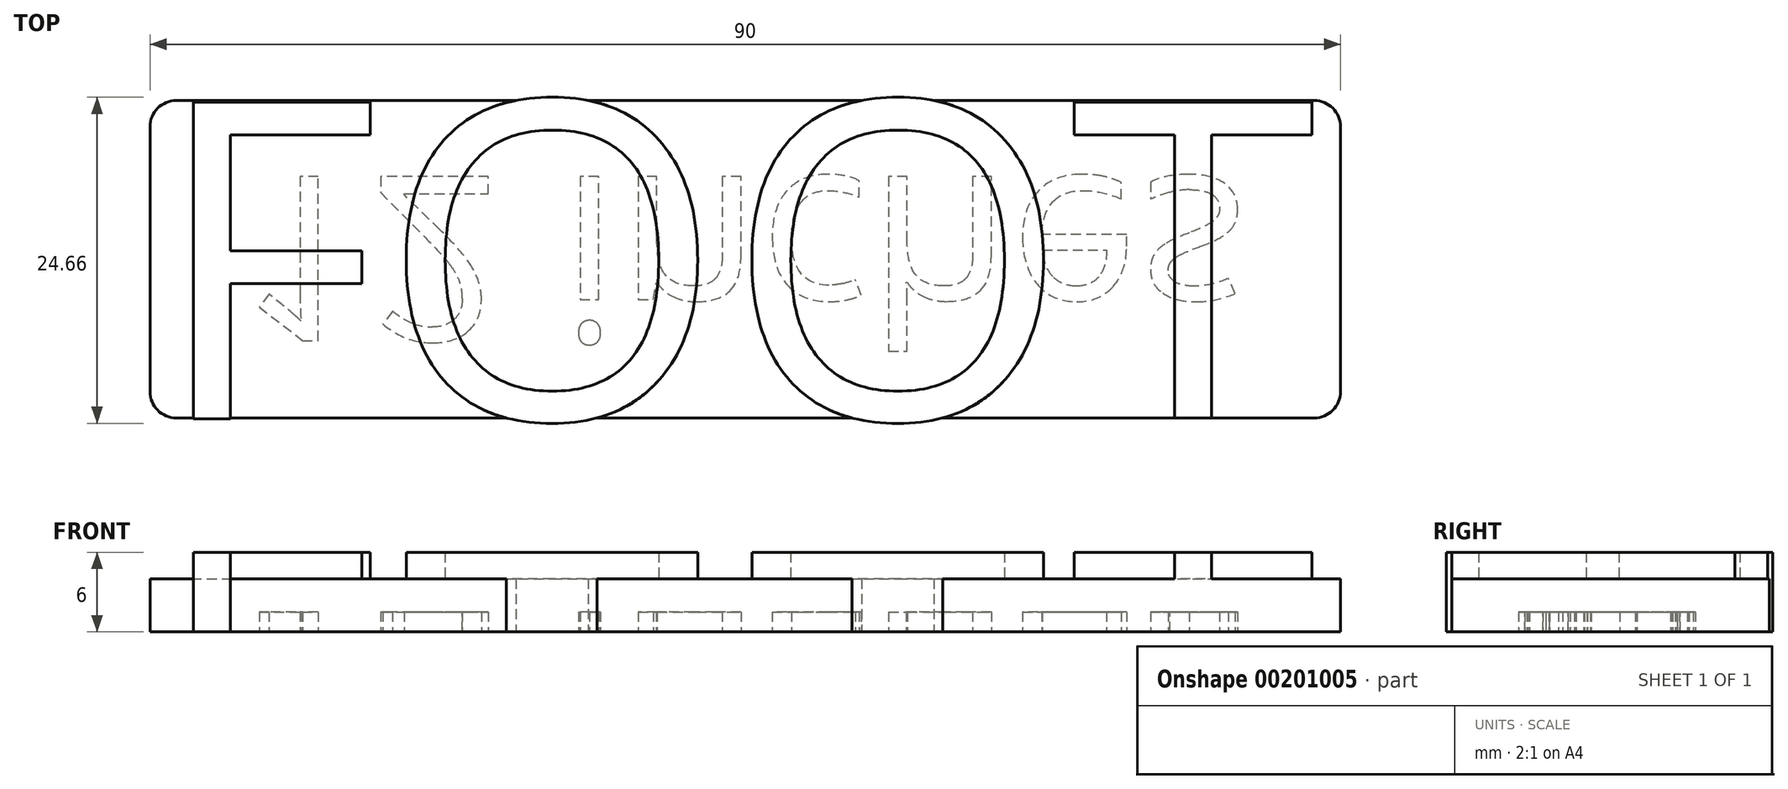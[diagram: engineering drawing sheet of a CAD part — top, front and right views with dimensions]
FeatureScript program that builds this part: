
annotation { "Feature Type Name" : "Feature", "Feature Type Description" : "" }
export const myFeature = defineFeature(function(context is Context, id is Id, definition is map)
    precondition{}
    {
        {
            var Q0;
            Q0=qCreatedBy(makeId("Top.planeOp"),FACE);
            var sketch = newSketch(context, id + "F0", { "sketchPlane" : qUnion([Q0])});
            skLineSegment(sketch, "E0.bottom", {"start": v(-45, 12) * mm, "end": v(45, 12) * mm});
            skLineSegment(sketch, "E0.top", {"start": v(-45, -12) * mm, "end": v(45, -12) * mm});
            skLineSegment(sketch, "E0.left", {"start": v(-45, 12) * mm, "end": v(-45, -12) * mm});
            skLineSegment(sketch, "E0.right", {"start": v(45, 12) * mm, "end": v(45, -12) * mm});
            skLineSegment(sketch, "E1", {"start": v(0, -12) * mm, "end": v(0, 12) * mm, "construction": true});
            skSolve(sketch);
        }
        {
            var Q0;
            Q0=makeQuery(id+"F0.imprint","IMPRINT",FACE,{"disambiguationData":[TD([[makeQuery(id+"F0.imprint","IMPRINT",EDGE,{"derivedFrom":sQuery(id+"F0.wireOp",EDGE,"E0.bottom")}),-1.0]])]});
            extrude(context, id + "F1", {"entities" : qUnion([Q0]), "depth" : 4 * mm});
        }
        {
            var Q0;
            Q0=makeQuery(id+"F1.opExtrude","SWEPT_EDGE",EDGE,{"disambiguationData":[OSD([sQuery(id+"F0.wireOp",EDGE,"E0.top"),sQuery(id+"F0.wireOp",EDGE,"E0.left")])]});
            var Q1;
            Q1=makeQuery(id+"F1.opExtrude","SWEPT_EDGE",EDGE,{"disambiguationData":[OSD([sQuery(id+"F0.wireOp",EDGE,"E0.bottom"),sQuery(id+"F0.wireOp",EDGE,"E0.right")])]});
            var Q2;
            Q2=makeQuery(id+"F1.opExtrude","SWEPT_EDGE",EDGE,{"disambiguationData":[OSD([sQuery(id+"F0.wireOp",EDGE,"E0.bottom"),sQuery(id+"F0.wireOp",EDGE,"E0.left")])]});
            var Q3;
            Q3=makeQuery(id+"F1.opExtrude","SWEPT_EDGE",EDGE,{"disambiguationData":[OSD([sQuery(id+"F0.wireOp",EDGE,"E0.top"),sQuery(id+"F0.wireOp",EDGE,"E0.right")])]});
            fillet(context, id + "F2", {"entities" : qUnion([Q0, Q1, Q2, Q3]), "radius" : 2 * mm, "tangentPropagation" : true, "allowEdgeOverflow" : false});
        }
        {
            var Q0;
            Q0=makeQuery(id+"F1.opExtrude","CAP_FACE",FACE,{"disambiguationData":[OSD([sQuery(id+"F0.wireOp",EDGE,"E0.bottom"),sQuery(id+"F0.wireOp",EDGE,"E0.top"),sQuery(id+"F0.wireOp",EDGE,"E0.left"),sQuery(id+"F0.wireOp",EDGE,"E0.right")])],"isStart":false});
            var sketch = newSketch(context, id + "F3", { "sketchPlane" : qUnion([Q0])});
            skText(sketch, "E2", { "text": "FOOT", "fontName": "OpenSans-Regular.ttf"});
            const initialGuessF3  = {"E2": [-0.045, -0.01208, 1, 0, 0.02416]};
            skSetInitialGuess(sketch, initialGuessF3);
            skSolve(sketch);
        }
        {
            var Q0;
            {var subQ0=sQuery(id+"F3.wireOp",EDGE,"E2.sketch_text.stroke-4");Q0=makeQuery(id+"F3.imprint","IMPRINT",FACE,{"disambiguationData":[TD([[makeQuery(id+"F3.imprint","IMPRINT",EDGE,{"derivedFrom":subQ0}),-1.0]])]});}
            var Q1;
            {var subQ0=sQuery(id+"F3.wireOp",EDGE,"E2.sketch_text.stroke-3");var subQ1=sQuery(id+"F3.wireOp",EDGE,"E2.sketch_text.stroke-2");var subQ2=makeQuery(id+"F3.imprint","INTERSECT",VERTEX,{"derivedFrom":[subQ1,subQ0]});Q1=makeQuery(id+"F3.imprint","IMPRINT",FACE,{"disambiguationData":[TD([[makeQuery(id+"F3.imprint","IMPRINT",EDGE,{"disambiguationData":[TD([[subQ2,1.0]])],"derivedFrom":subQ1}),-1.0]])]});}
            var Q2;
            {var subQ1=sQuery(id+"F3.wireOp",EDGE,"E2.sketch_text.stroke-1");Q2=makeQuery(id+"F3.imprint","IMPRINT",FACE,{"disambiguationData":[TD([[makeQuery(id+"F3.imprint","IMPRINT",EDGE,{"derivedFrom":subQ1}),-1.0]])]});}
            var Q3;
            {var subQ0=sQuery(id+"F3.wireOp",EDGE,"E2.sketch_text.stroke-0");var subQ1=makeQuery(id+"F1.opExtrude","CAP_EDGE",EDGE,{"disambiguationData":[OSD([sQuery(id+"F0.wireOp",EDGE,"E0.top")])],"isStart":false});var subQ2=makeQuery(id+"F3.imprint","INTERSECT",VERTEX,{"derivedFrom":[subQ1,subQ0]});Q3=makeQuery(id+"F3.imprint","IMPRINT",FACE,{"disambiguationData":[TD([[makeQuery(id+"F3.imprint","IMPRINT",EDGE,{"disambiguationData":[TD([[subQ2,-1.0]])],"derivedFrom":subQ0}),-1.0]])]});}
            var Q4;
            {var subQ1=sQuery(id+"F3.wireOp",EDGE,"E2.sketch_text.stroke-8");Q4=makeQuery(id+"F3.imprint","IMPRINT",FACE,{"disambiguationData":[TD([[makeQuery(id+"F3.imprint","IMPRINT",EDGE,{"derivedFrom":subQ1}),-1.0]])]});}
            var Q5;
            {var subQ0=sQuery(id+"F3.wireOp",EDGE,"E2.sketch_text.stroke-9");var subQ1=makeQuery(id+"F1.opExtrude","CAP_EDGE",EDGE,{"disambiguationData":[OSD([sQuery(id+"F0.wireOp",EDGE,"E0.bottom")])],"isStart":false});var subQ2=makeQuery(id+"F3.imprint","INTERSECT",VERTEX,{"derivedFrom":[subQ1,subQ0]});Q5=makeQuery(id+"F3.imprint","IMPRINT",FACE,{"disambiguationData":[TD([[makeQuery(id+"F3.imprint","IMPRINT",EDGE,{"disambiguationData":[TD([[subQ2,1.0]])],"derivedFrom":subQ0}),-1.0]])]});}
            var Q6;
            {var subQ1=sQuery(id+"F3.wireOp",EDGE,"E2.sketch_text.stroke-10");Q6=makeQuery(id+"F3.imprint","IMPRINT",FACE,{"disambiguationData":[TD([[makeQuery(id+"F3.imprint","IMPRINT",EDGE,{"derivedFrom":subQ1}),-1.0]])]});}
            var Q7;
            {var subQ0=sQuery(id+"F3.wireOp",EDGE,"E2.sketch_text.stroke-11");var subQ1=makeQuery(id+"F1.opExtrude","CAP_EDGE",EDGE,{"disambiguationData":[OSD([sQuery(id+"F0.wireOp",EDGE,"E0.bottom")])],"isStart":false});var subQ2=makeQuery(id+"F3.imprint","INTERSECT",VERTEX,{"derivedFrom":[subQ1,subQ0]});Q7=makeQuery(id+"F3.imprint","IMPRINT",FACE,{"disambiguationData":[TD([[makeQuery(id+"F3.imprint","IMPRINT",EDGE,{"disambiguationData":[TD([[subQ2,-1.0]])],"derivedFrom":subQ0}),-1.0]])]});}
            var Q8;
            {var subQ0=sQuery(id+"F3.wireOp",EDGE,"E2.sketch_text.stroke-12");Q8=makeQuery(id+"F3.imprint","IMPRINT",FACE,{"disambiguationData":[TD([[makeQuery(id+"F3.imprint","IMPRINT",EDGE,{"derivedFrom":subQ0}),-1.0]])]});}
            var Q9;
            {var subQ0=sQuery(id+"F3.wireOp",EDGE,"E2.sketch_text.stroke-21");Q9=makeQuery(id+"F3.imprint","IMPRINT",FACE,{"disambiguationData":[TD([[makeQuery(id+"F3.imprint","IMPRINT",EDGE,{"derivedFrom":subQ0}),-1.0]])]});}
            var Q10;
            {var subQ0=sQuery(id+"F3.wireOp",EDGE,"E2.sketch_text.stroke-18");var subQ1=makeQuery(id+"F1.opExtrude","CAP_EDGE",EDGE,{"disambiguationData":[OSD([sQuery(id+"F0.wireOp",EDGE,"E0.top")])],"isStart":false});var subQ2=makeQuery(id+"F3.imprint","INTERSECT",VERTEX,{"derivedFrom":[subQ1,subQ0]});Q10=makeQuery(id+"F3.imprint","IMPRINT",FACE,{"disambiguationData":[TD([[makeQuery(id+"F3.imprint","IMPRINT",EDGE,{"disambiguationData":[TD([[subQ2,-1.0]])],"derivedFrom":subQ0}),-1.0]])]});}
            var Q11;
            {var subQ0=sQuery(id+"F3.wireOp",EDGE,"E2.sketch_text.stroke-19");Q11=makeQuery(id+"F3.imprint","IMPRINT",FACE,{"disambiguationData":[TD([[makeQuery(id+"F3.imprint","IMPRINT",EDGE,{"derivedFrom":subQ0}),-1.0]])]});}
            var Q12;
            {var subQ0=sQuery(id+"F3.wireOp",EDGE,"E2.sketch_text.stroke-25");Q12=makeQuery(id+"F3.imprint","IMPRINT",FACE,{"disambiguationData":[TD([[makeQuery(id+"F3.imprint","IMPRINT",EDGE,{"derivedFrom":subQ0}),-1.0]])]});}
            var Q13;
            {var subQ0=sQuery(id+"F3.wireOp",EDGE,"E2.sketch_text.stroke-22");var subQ1=makeQuery(id+"F1.opExtrude","CAP_EDGE",EDGE,{"disambiguationData":[OSD([sQuery(id+"F0.wireOp",EDGE,"E0.top")])],"isStart":false});var subQ2=makeQuery(id+"F3.imprint","INTERSECT",VERTEX,{"derivedFrom":[subQ1,subQ0]});Q13=makeQuery(id+"F3.imprint","IMPRINT",FACE,{"disambiguationData":[TD([[makeQuery(id+"F3.imprint","IMPRINT",EDGE,{"disambiguationData":[TD([[subQ2,-1.0]])],"derivedFrom":subQ0}),-1.0]])]});}
            var Q14;
            {var subQ0=sQuery(id+"F3.wireOp",EDGE,"E2.sketch_text.stroke-23");Q14=makeQuery(id+"F3.imprint","IMPRINT",FACE,{"disambiguationData":[TD([[makeQuery(id+"F3.imprint","IMPRINT",EDGE,{"derivedFrom":subQ0}),-1.0]])]});}
            var Q15;
            {var subQ5=sQuery(id+"F3.wireOp",EDGE,"E2.sketch_text.stroke-28");Q15=makeQuery(id+"F3.imprint","IMPRINT",FACE,{"disambiguationData":[TD([[makeQuery(id+"F3.imprint","IMPRINT",EDGE,{"derivedFrom":subQ5}),-1.0]])]});}
            var Q16;
            {var subQ0=sQuery(id+"F3.wireOp",EDGE,"E2.sketch_text.stroke-34");Q16=makeQuery(id+"F3.imprint","IMPRINT",FACE,{"disambiguationData":[TD([[makeQuery(id+"F3.imprint","IMPRINT",EDGE,{"derivedFrom":subQ0}),-1.0]])]});}
            var Q17;
            {var subQ0=sQuery(id+"F3.wireOp",EDGE,"E2.sketch_text.stroke-30");Q17=makeQuery(id+"F3.imprint","IMPRINT",FACE,{"disambiguationData":[TD([[makeQuery(id+"F3.imprint","IMPRINT",EDGE,{"derivedFrom":subQ0}),-1.0]])]});}
            var Q18;
            {var subQ0=sQuery(id+"F3.wireOp",EDGE,"E2.sketch_text.stroke-6");Q18=makeQuery(id+"F3.imprint","IMPRINT",FACE,{"disambiguationData":[TD([[makeQuery(id+"F3.imprint","IMPRINT",EDGE,{"derivedFrom":subQ0}),-1.0]])]});}
            var Q19;
            {var subQ0=sQuery(id+"F3.wireOp",EDGE,"E2.sketch_text.stroke-17");Q19=makeQuery(id+"F3.imprint","IMPRINT",FACE,{"disambiguationData":[TD([[makeQuery(id+"F3.imprint","IMPRINT",EDGE,{"derivedFrom":subQ0}),-1.0]])]});}
            var Q20;
            {var subQ0=sQuery(id+"F3.wireOp",EDGE,"E2.sketch_text.stroke-27");Q20=makeQuery(id+"F3.imprint","IMPRINT",FACE,{"disambiguationData":[TD([[makeQuery(id+"F3.imprint","IMPRINT",EDGE,{"derivedFrom":subQ0}),-1.0]])]});}
            var Q21;
            {var subQ0=sQuery(id+"F3.wireOp",EDGE,"E2.sketch_text.stroke-16");var subQ1=sQuery(id+"F3.wireOp",EDGE,"E2.sketch_text.stroke-15");var subQ2=makeQuery(id+"F3.imprint","INTERSECT",VERTEX,{"derivedFrom":[subQ1,subQ0]});Q21=makeQuery(id+"F3.imprint","IMPRINT",FACE,{"disambiguationData":[TD([[makeQuery(id+"F3.imprint","IMPRINT",EDGE,{"disambiguationData":[TD([[subQ2,1.0]])],"derivedFrom":subQ1}),-1.0]])]});}
            var Q22;
            {var subQ0=sQuery(id+"F3.wireOp",EDGE,"E2.sketch_text.stroke-32");var subQ1=sQuery(id+"F3.wireOp",EDGE,"E2.sketch_text.stroke-31");var subQ2=makeQuery(id+"F3.imprint","INTERSECT",VERTEX,{"derivedFrom":[subQ1,subQ0]});Q22=makeQuery(id+"F3.imprint","IMPRINT",FACE,{"disambiguationData":[TD([[makeQuery(id+"F3.imprint","IMPRINT",EDGE,{"disambiguationData":[TD([[subQ2,1.0]])],"derivedFrom":subQ1}),-1.0]])]});}
            var Q23;
            {var subQ1=sQuery(id+"F3.wireOp",EDGE,"E2.sketch_text.stroke-44");Q23=makeQuery(id+"F3.imprint","IMPRINT",FACE,{"disambiguationData":[TD([[makeQuery(id+"F3.imprint","IMPRINT",EDGE,{"derivedFrom":subQ1}),-1.0]])]});}
            extrude(context, id + "F4", {"entities" : qUnion([Q0, Q1, Q2, Q3, Q4, Q5, Q6, Q7, Q8, Q9, Q10, Q11, Q12, Q13, Q14, Q15, Q16, Q17, Q18, Q19, Q20, Q21, Q22, Q23]), "operationType" : NewBodyOperationType.ADD, "depth" : 2 * mm, "hasSecondDirection" : true, "secondDirectionOppositeDirection" : true, "secondDirectionDepth" : 4 * mm});
        }
        {
            var Q0;
            Q0=makeQuery(id+"F1.opExtrude","CAP_FACE",FACE,{"disambiguationData":[OSD([sQuery(id+"F0.wireOp",EDGE,"E0.bottom"),sQuery(id+"F0.wireOp",EDGE,"E0.top"),sQuery(id+"F0.wireOp",EDGE,"E0.left"),sQuery(id+"F0.wireOp",EDGE,"E0.right")])],"isStart":true});
            var sketch = newSketch(context, id + "F5", { "sketchPlane" : qUnion([Q0])});
            skText(sketch, "E3", { "text": "12 inches", "fontName": "OpenSans-Regular.ttf"});
            const initialGuessF5  = {"E3": [-0.03834, -0.00625, 1, 0, 0.0125]};
            skSetInitialGuess(sketch, initialGuessF5);
            skSolve(sketch);
        }
        {
            var Q0;
            Q0=makeQuery(id+"F5.imprint","IMPRINT",FACE,{"disambiguationData":[TD([[makeQuery(id+"F5.imprint","IMPRINT",EDGE,{"derivedFrom":sQuery(id+"F5.wireOp",EDGE,"E3.sketch_text.stroke-122")}),-1.0]])]});
            var Q1;
            Q1=makeQuery(id+"F5.imprint","IMPRINT",FACE,{"disambiguationData":[TD([[makeQuery(id+"F5.imprint","IMPRINT",EDGE,{"derivedFrom":sQuery(id+"F5.wireOp",EDGE,"E3.sketch_text.stroke-103")}),-1.0]])]});
            var Q2;
            Q2=makeQuery(id+"F5.imprint","IMPRINT",FACE,{"disambiguationData":[TD([[makeQuery(id+"F5.imprint","IMPRINT",EDGE,{"derivedFrom":sQuery(id+"F5.wireOp",EDGE,"E3.sketch_text.stroke-86")}),-1.0]])]});
            var Q3;
            Q3=makeQuery(id+"F5.imprint","IMPRINT",FACE,{"disambiguationData":[TD([[makeQuery(id+"F5.imprint","IMPRINT",EDGE,{"derivedFrom":sQuery(id+"F5.wireOp",EDGE,"E3.sketch_text.stroke-70")}),-1.0]])]});
            var Q4;
            Q4=makeQuery(id+"F5.imprint","IMPRINT",FACE,{"disambiguationData":[TD([[makeQuery(id+"F5.imprint","IMPRINT",EDGE,{"derivedFrom":sQuery(id+"F5.wireOp",EDGE,"E3.sketch_text.stroke-39")}),-1.0]])]});
            var Q5;
            Q5=makeQuery(id+"F5.imprint","IMPRINT",FACE,{"disambiguationData":[TD([[makeQuery(id+"F5.imprint","IMPRINT",EDGE,{"derivedFrom":sQuery(id+"F5.wireOp",EDGE,"E3.sketch_text.stroke-19")}),-1.0]])]});
            var Q6;
            Q6=makeQuery(id+"F5.imprint","IMPRINT",FACE,{"disambiguationData":[TD([[makeQuery(id+"F5.imprint","IMPRINT",EDGE,{"derivedFrom":sQuery(id+"F5.wireOp",EDGE,"E3.sketch_text.stroke-0")}),-1.0]])]});
            var Q7;
            Q7=makeQuery(id+"F5.imprint","IMPRINT",FACE,{"disambiguationData":[TD([[makeQuery(id+"F5.imprint","IMPRINT",EDGE,{"derivedFrom":sQuery(id+"F5.wireOp",EDGE,"E3.sketch_text.stroke-41")}),-1.0]])]});
            var Q8;
            Q8=makeQuery(id+"F5.imprint","IMPRINT",FACE,{"disambiguationData":[TD([[makeQuery(id+"F5.imprint","IMPRINT",EDGE,{"derivedFrom":sQuery(id+"F5.wireOp",EDGE,"E3.sketch_text.stroke-29")}),-1.0]])]});
            extrude(context, id + "F6", {"entities" : qUnion([Q0, Q1, Q2, Q3, Q4, Q5, Q6, Q7, Q8]), "operationType" : NewBodyOperationType.REMOVE, "oppositeDirection" : true, "depth" : 1.5 * mm});
        }
    });
